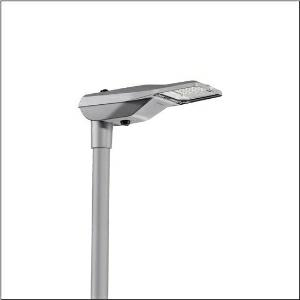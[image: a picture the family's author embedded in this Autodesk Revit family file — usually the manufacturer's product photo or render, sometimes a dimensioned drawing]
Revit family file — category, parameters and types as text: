
# Revit family: streetlight_sl_21_micro___p0_8ab_5xe1r33t08db_81a7
name_source: partatom
category: Lighting Fixtures
units: mm (PartAtom-declared; Revit-internal decimal feet)

## family parameters
Cut with Voids When Loaded = No
Host = Face
Light Source = No
Part Type = Normal
Room Calculation Point = No
Round Connector Dimension = Use Diameter
Shared = No

## types (1)
- --- (1 x LED, 4470 lm, 39.1 W, 3000K)
    Apparent Load = 39 VA
    CIE Flux Codes = 36 71 98 100 100
    Color Rendering = 70
    Color Temperature = 3000K
    Default Elevation = 1800 mm
    Description = Streetlight SL 21 micro, mast luminaire, primary light control with lens, of PMMA, primary optical cover: cover, of toughened safety glass, transparent, light distribution: P0.8aB, light emission: direct distribution, primary light characteristic: asymmetric, installation type: post-top, side-entry, LED, High Power LED, rated luminous flux: 4.470lm, luminous efficacy: 114lm/W, light colour: 730, colour temperature: 3000K, control gear: D4i, control: pre-setting: logarithmic dimming characteristic, flexible luminous flux parameterisation, time-dependent luminous flux control, constant luminous flux control, overheat protection, mains connection: 220..240V, AC, 50/60Hz, start of lifetime: 39W, end of service life: 41W, reduction: 18W, luminaire housing, of diecast aluminium, powder-coated, Siteco® metallic grey (DB 702S), corrosivity category C5 mid according to DIN EN ISO 12944, multi-level sealing system, sealing non-destructively replaceable, inclination adjustable: 0°, 5°, 10°, 15°, please order mast flange separately, length: 528mm, width: 235mm, height: 110mm, mast flange for spigot size: 42mm (side-entry): 5XC10008XM4, 60/48mm (side-entry/post-top): 5XC10108XM2, 76/60mm (side-entry/post-top): 5XC10108XM1, Smart Interface below and above, protection rating (complete): IP66, insulation class (complete): insulation class II (safety insulation), certification: CE, ENEC, ENEC+, VDE, impact resistance: IK10, permissible operating ambient temperature for outdoor applications: -40..+50°C, standard-compliant lighting for roads and squares, packaging unit: 1 piece

Light Distribution: P0.8aB
    Height = 110 mm
    Lamp = 1 x LED
    Lamp Light Flux = 4470 lm
    Lamp Power = 39.1 W
    Lamp count = 1
    Length = 528 mm
    Luminous efficacy = 114 lm/W
    Manufacturer = Siteco
    ModVariant = No
    Model = 5XE1R33T08DB
    Number of Poles = 1
    OnlyDefault = Yes
    Power Factor = 1
    Product Name = Streetlight SL 21 micro | P0.8aB
    Product group = mast luminaire | pylon top
    ProductGroupID = 6100
    Protection Class = Protection class II
    Protection Degree = IP 66
    RLX_Detail_Level = 1
    RLX_Emergency_Light_Flux = 0 lm
    RLX_Emergency_Type = 0
    RLX_Emergency_Type_DB = No
    RlxData = <blob elided: 98521 chars, md5=59c46192>
    Socket = socket
    Standby Power = 0 W
    System Light Flux = 4470 lm
    System Power = 39 W
    Type Comments = factory setting: luminous flux: 100 % | dim-lin: 254 | 765 mA
    Type Image = l_1007239.jpg
    URL = http://relux.com
    VarID = @adj_075082
    Voltage = 0 V
    Weight = 0.00 kg
    Width = 235 mm

## geometry (parser evidence)
native form markers: Blend x4, Sweep x11
no freeform markers — native parametric forms only
